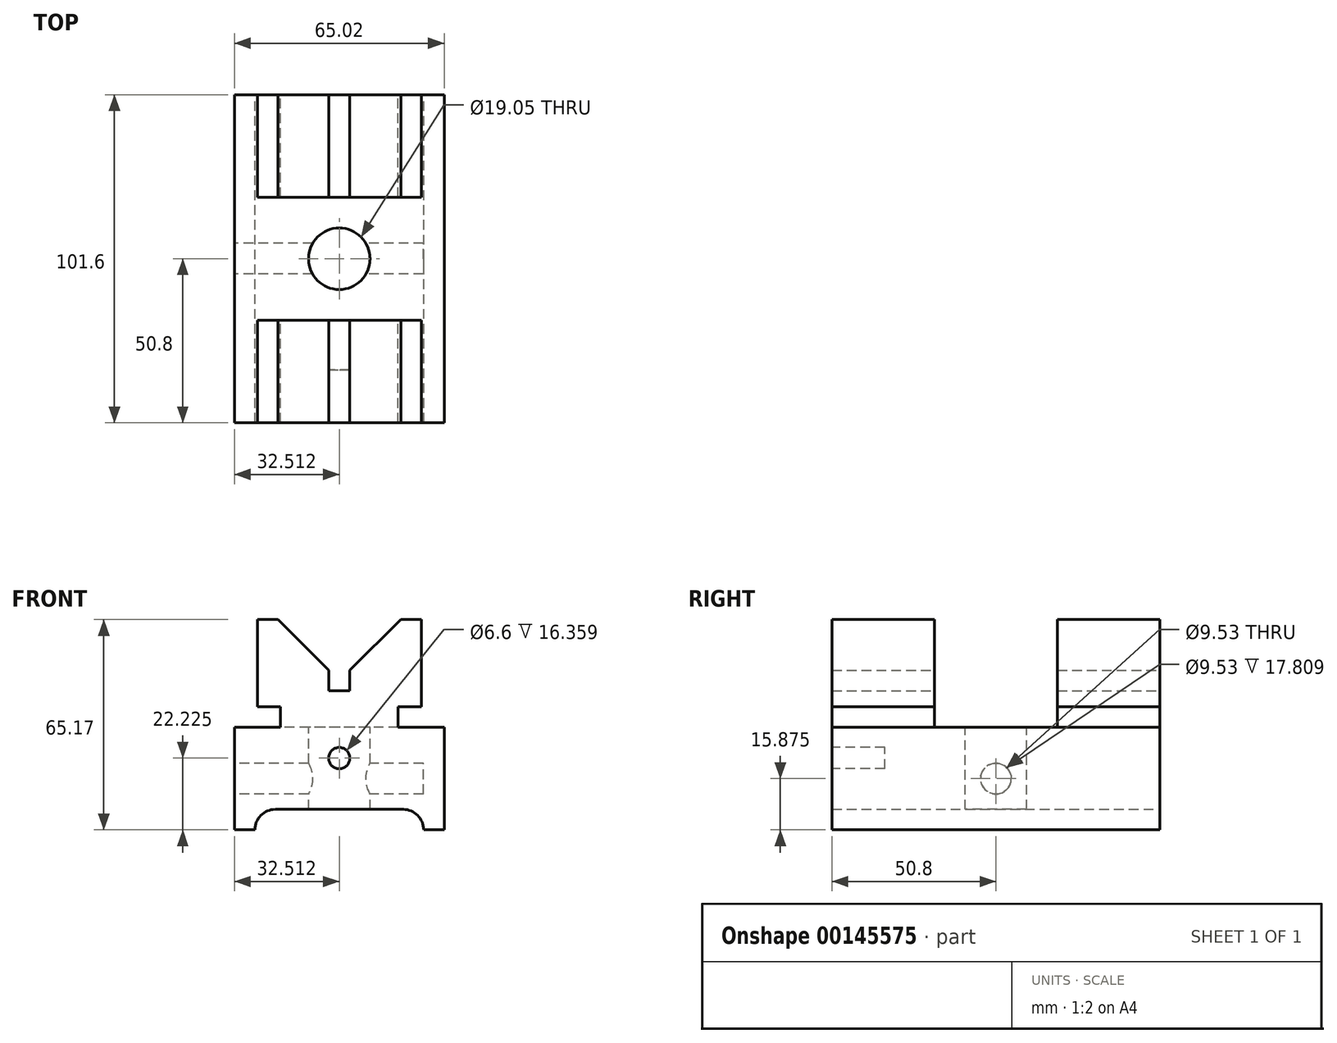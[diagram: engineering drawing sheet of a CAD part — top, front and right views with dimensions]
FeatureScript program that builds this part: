
annotation { "Feature Type Name" : "Feature", "Feature Type Description" : "" }
export const myFeature = defineFeature(function(context is Context, id is Id, definition is map)
    precondition{}
    {
        {
            var Q0;
            Q0=qCreatedBy(makeId("Front.planeOp"),FACE);
            var sketch = newSketch(context, id + "F0", { "sketchPlane" : qUnion([Q0])});
            skLineSegment(sketch, "E0", {"start": v(6.35, 0) * mm, "end": v(0, 0) * mm});
            skLineSegment(sketch, "E1", {"start": v(0, 0) * mm, "end": v(0, 31.75) * mm});
            skLineSegment(sketch, "E2", {"start": v(0, 31.75) * mm, "end": v(14.22, 31.75) * mm});
            skLineSegment(sketch, "E3", {"start": v(14.22, 31.75) * mm, "end": v(14.22, 38.1) * mm});
            skLineSegment(sketch, "E4", {"start": v(14.22, 38.1) * mm, "end": v(7.11, 38.1) * mm});
            skLineSegment(sketch, "E5", {"start": v(7.11, 38.1) * mm, "end": v(7.11, 65.17) * mm});
            skLineSegment(sketch, "E6", {"start": v(7.11, 65.17) * mm, "end": v(13.46, 65.17) * mm});
            skLineSegment(sketch, "E7", {"start": v(13.46, 65.17) * mm, "end": v(29.21, 49.43) * mm});
            skLineSegment(sketch, "E8", {"start": v(29.21, 49.43) * mm, "end": v(29.21, 43.08) * mm});
            skLineSegment(sketch, "E9", {"start": v(29.21, 43.08) * mm, "end": v(35.81, 43.08) * mm});
            skLineSegment(sketch, "E10", {"start": v(35.81, 43.08) * mm, "end": v(35.81, 49.43) * mm});
            skLineSegment(sketch, "E11", {"start": v(35.81, 49.43) * mm, "end": v(51.56, 65.17) * mm});
            skLineSegment(sketch, "E12", {"start": v(51.56, 65.17) * mm, "end": v(57.91, 65.17) * mm});
            skLineSegment(sketch, "E13", {"start": v(57.91, 65.17) * mm, "end": v(57.91, 38.1) * mm});
            skLineSegment(sketch, "E14", {"start": v(57.91, 38.1) * mm, "end": v(50.8, 38.1) * mm});
            skLineSegment(sketch, "E15", {"start": v(50.8, 38.1) * mm, "end": v(50.8, 31.75) * mm});
            skLineSegment(sketch, "E16", {"start": v(50.8, 31.75) * mm, "end": v(65.02, 31.75) * mm});
            skLineSegment(sketch, "E17", {"start": v(65.02, 31.75) * mm, "end": v(65.02, 0) * mm});
            skLineSegment(sketch, "E18", {"start": v(65.02, 0) * mm, "end": v(58.67, 0) * mm});
            skLineSegment(sketch, "E19", {"start": v(12.7, 6.35) * mm, "end": v(52.32, 6.35) * mm});
            skArc(sketch, "E20", {"start": v(12.7, 6.35) * mm, "mid": v(8.2, 4.5) * mm, "end": v(6.35, 0) * mm});
            skArc(sketch, "E21", {"start": v(58.67, 0) * mm, "mid": v(56.81, 4.5) * mm, "end": v(52.32, 6.35) * mm});
            skLineSegment(sketch, "E22", {"start": v(32.51, 0) * mm, "end": v(32.51, 73.7) * mm, "construction": true});
            skCircle(sketch, "E23", {"center": v(32.51, 22.23) * mm, "radius": 3.3 * mm});
            skSolve(sketch);
        }
        {
            var Q0;
            Q0 = qSketchRegion(id + "F0", true);
            var Q1;
            Q1=makeQuery(id+"F0.imprint","IMPRINT",FACE,{"disambiguationData":[TD([[makeQuery(id+"F0.imprint","IMPRINT",EDGE,{"derivedFrom":sQuery(id+"F0.wireOp",EDGE,"E23")}),1.0]])]});
            extrude(context, id + "F1", {"entities" : qUnion([Q0, Q1]), "depth" : 101.6 * mm});
        }
        {
            var Q0;
            Q0=makeQuery(id+"F1.opExtrude","CAP_FACE",FACE,{"disambiguationData":[OSD([sQuery(id+"F0.wireOp",EDGE,"E0"),sQuery(id+"F0.wireOp",EDGE,"E1"),sQuery(id+"F0.wireOp",EDGE,"E2"),sQuery(id+"F0.wireOp",EDGE,"E3"),sQuery(id+"F0.wireOp",EDGE,"E4"),sQuery(id+"F0.wireOp",EDGE,"E5"),sQuery(id+"F0.wireOp",EDGE,"E6"),sQuery(id+"F0.wireOp",EDGE,"E7"),sQuery(id+"F0.wireOp",EDGE,"E8"),sQuery(id+"F0.wireOp",EDGE,"E9"),sQuery(id+"F0.wireOp",EDGE,"E10"),sQuery(id+"F0.wireOp",EDGE,"E11"),sQuery(id+"F0.wireOp",EDGE,"E12"),sQuery(id+"F0.wireOp",EDGE,"E13"),sQuery(id+"F0.wireOp",EDGE,"E14"),sQuery(id+"F0.wireOp",EDGE,"E15"),sQuery(id+"F0.wireOp",EDGE,"E16"),sQuery(id+"F0.wireOp",EDGE,"E17"),sQuery(id+"F0.wireOp",EDGE,"E18"),sQuery(id+"F0.wireOp",EDGE,"E19"),sQuery(id+"F0.wireOp",EDGE,"E20"),sQuery(id+"F0.wireOp",EDGE,"E21")])],"isStart":false});
            var sketch = newSketch(context, id + "F2", { "sketchPlane" : qUnion([Q0])});
            skCircle(sketch, "E24.0", {"center": v(32.51, 22.23) * mm, "radius": 3.3 * mm});
            skSolve(sketch);
        }
        {
            var Q0;
            Q0 = qSketchRegion(id + "F2", true);
            extrude(context, id + "F3", {"entities" : qUnion([Q0]), "operationType" : NewBodyOperationType.REMOVE, "oppositeDirection" : true, "depth" : 16.36 * mm});
        }
        {
            var Q0;
            Q0=qCreatedBy(makeId("Right.planeOp"),FACE);
            var sketch = newSketch(context, id + "F4", { "sketchPlane" : qUnion([Q0])});
            skLineSegment(sketch, "E25", {"start": v(-31.75, 65.17) * mm, "end": v(-31.75, 31.75) * mm});
            skLineSegment(sketch, "E26", {"start": v(-69.85, 65.17) * mm, "end": v(-69.85, 31.75) * mm});
            skCircle(sketch, "E27", {"center": v(-50.8, 15.88) * mm, "radius": 4.76 * mm});
            skLineSegment(sketch, "E28.0", {"start": v(-101.6, 31.75) * mm, "end": v(0, 31.75) * mm});
            skLineSegment(sketch, "E29.0", {"start": v(-101.6, 65.17) * mm, "end": v(0, 65.17) * mm});
            skLineSegment(sketch, "E30.0", {"start": v(-101.6, 0) * mm, "end": v(0, 0) * mm});
            skSolve(sketch);
        }
        {
            var Q0;
            Q0 = qSketchRegion(id + "F4", true);
            extrude(context, id + "F5", {"entities" : qUnion([Q0]), "operationType" : NewBodyOperationType.REMOVE, "depth" : 58.57 * mm});
        }
        {
            var Q0;
            Q0=makeQuery(id+"F5.boolean.opBoolean","MERGE",FACE,{"derivedFrom":[makeQuery(id+"F1.opExtrude","SWEPT_FACE",FACE,{"disambiguationData":[OSD([sQuery(id+"F0.wireOp",EDGE,"E2")])]}),makeQuery(id+"F1.opExtrude","SWEPT_FACE",FACE,{"disambiguationData":[OSD([sQuery(id+"F0.wireOp",EDGE,"E16")])]}),makeQuery(id+"F5.opExtrude","SWEPT_FACE",FACE,{"disambiguationData":[OSD([sQuery(id+"F4.wireOp",EDGE,"E28.0")])]})]});
            var sketch = newSketch(context, id + "F6", { "sketchPlane" : qUnion([Q0])});
            skCircle(sketch, "E31", {"center": v(32.51, -50.8) * mm, "radius": 9.53 * mm});
            skSolve(sketch);
        }
        {
            var Q0;
            Q0 = qSketchRegion(id + "F6", true);
            extrude(context, id + "F7", {"entities" : qUnion([Q0]), "operationType" : NewBodyOperationType.REMOVE, "endBound" : BoundingType.THROUGH_ALL, "oppositeDirection" : true, "depth" : 25.4 * mm});
        }
    });
